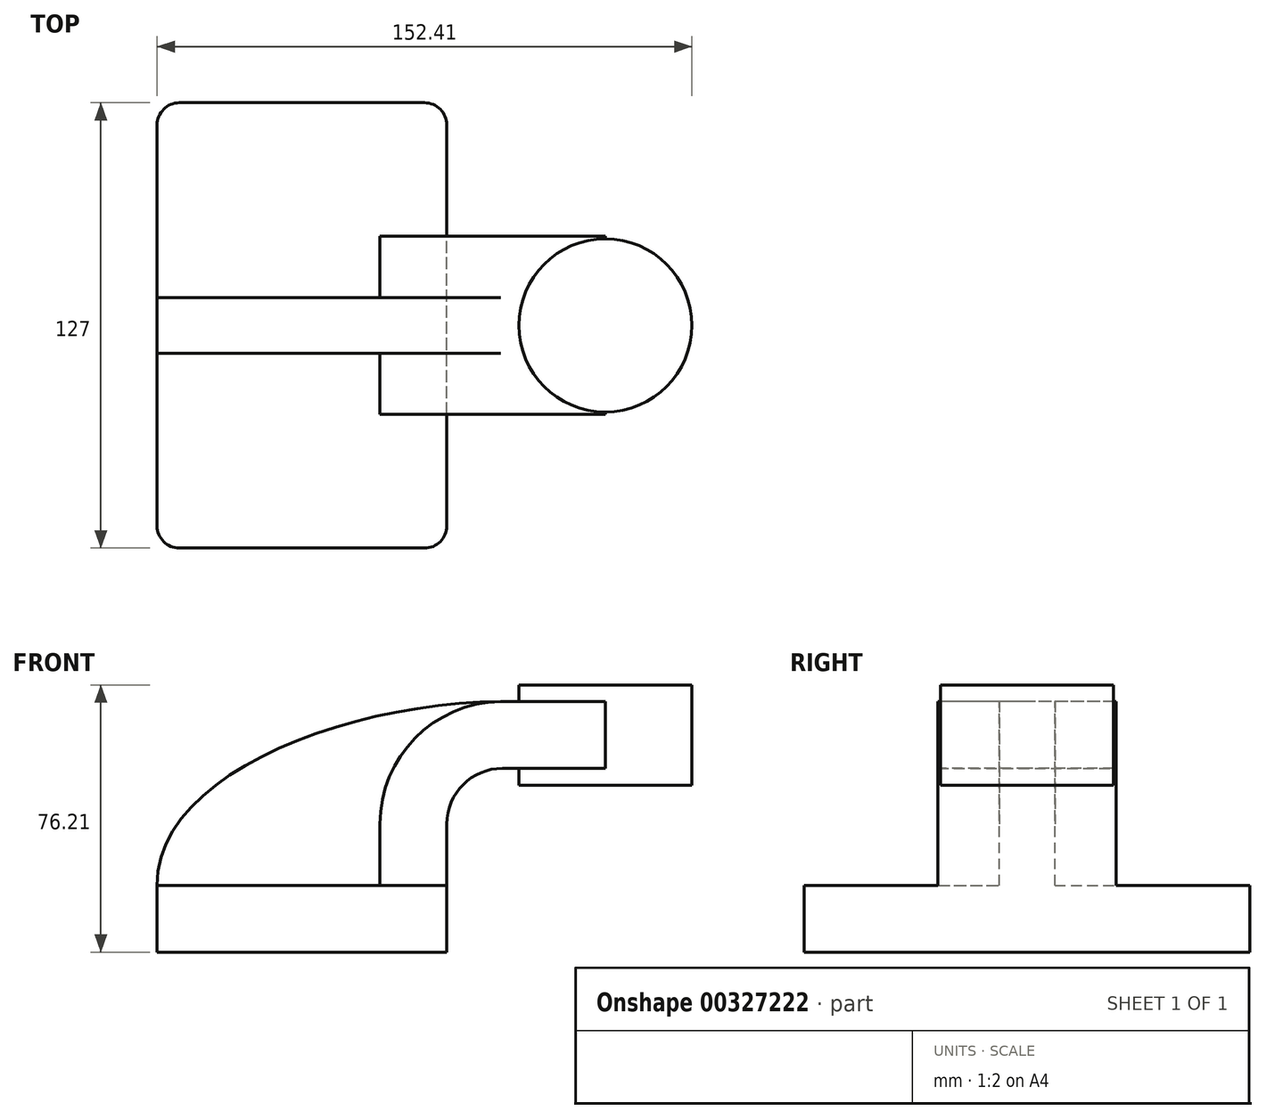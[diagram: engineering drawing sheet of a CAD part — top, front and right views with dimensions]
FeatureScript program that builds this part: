
annotation { "Feature Type Name" : "Feature", "Feature Type Description" : "" }
export const myFeature = defineFeature(function(context is Context, id is Id, definition is map)
    precondition{}
    {
        {
            var Q0;
            Q0=qCreatedBy(makeId("Front.planeOp"),FACE);
            var sketch = newSketch(context, id + "F0", { "sketchPlane" : qUnion([Q0])});
            skLineSegment(sketch, "E0.bottom", {"start": v(-41.28, 9.52) * mm, "end": v(41.27, 9.53) * mm});
            skLineSegment(sketch, "E0.top", {"start": v(-41.28, -9.53) * mm, "end": v(41.28, -9.53) * mm});
            skLineSegment(sketch, "E0.left", {"start": v(-41.28, 9.52) * mm, "end": v(-41.27, -9.53) * mm});
            skLineSegment(sketch, "E0.right", {"start": v(41.28, 9.53) * mm, "end": v(41.28, -9.52) * mm});
            skPoint(sketch, "E0.middle", {"position": v(0, 0) * mm});
            skLineSegment(sketch, "E1.bottom", {"start": v(60.33, 38.1) * mm, "end": v(111.12, 38.1) * mm});
            skLineSegment(sketch, "E1.top", {"start": v(60.32, 66.67) * mm, "end": v(111.12, 66.67) * mm});
            skLineSegment(sketch, "E1.left", {"start": v(60.33, 38.1) * mm, "end": v(60.32, 66.67) * mm});
            skLineSegment(sketch, "E1.right", {"start": v(111.13, 38.1) * mm, "end": v(111.12, 66.67) * mm});
            skPoint(sketch, "E1.middle", {"position": v(85.72, 52.39) * mm});
            skLineSegment(sketch, "E2", {"start": v(41.27, 9.53) * mm, "end": v(41.27, 27) * mm});
            skArc(sketch, "E3", {"start": v(41.27, 27) * mm, "mid": v(45.92, 38.23) * mm, "end": v(57.15, 42.88) * mm});
            skLineSegment(sketch, "E4", {"start": v(57.15, 42.88) * mm, "end": v(86.46, 42.88) * mm});
            skLineSegment(sketch, "E5.0", {"start": v(57.15, 61.93) * mm, "end": v(86.46, 61.93) * mm});
            skArc(sketch, "E5.1", {"start": v(22.23, 27) * mm, "mid": v(32.45, 51.7) * mm, "end": v(57.15, 61.93) * mm});
            skLineSegment(sketch, "E5.2", {"start": v(22.22, 9.53) * mm, "end": v(22.22, 27) * mm});
            skLineSegment(sketch, "E6", {"start": v(86.46, 38.1) * mm, "end": v(86.46, 66.67) * mm});
            skFitSpline(sketch, "E7", {"points": [v(-41.28, 9.53) * mm, v(57.15, 61.93) * mm], "startDerivative": vector(-0.4, 95.36) * mm, "endDerivative": vector(133.86, 0.83) * mm});
            skSolve(sketch);
        }
        {
            var Q0;
            Q0=makeQuery(id+"F0.imprint","IMPRINT",FACE,{"disambiguationData":[TD([[makeQuery(id+"F0.imprint","IMPRINT",EDGE,{"derivedFrom":sQuery(id+"F0.wireOp",EDGE,"E0.top")}),1.0]])]});
            extrude(context, id + "F1", {"entities" : qUnion([Q0]), "endBound" : BoundingType.SYMMETRIC, "depth" : 127 * mm});
        }
        {
            var Q0;
            {var subQ1=sQuery(id+"F0.wireOp",EDGE,"E2");Q0=makeQuery(id+"F0.imprint","IMPRINT",FACE,{"disambiguationData":[TD([[makeQuery(id+"F0.imprint","IMPRINT",EDGE,{"derivedFrom":subQ1}),1.0]])]});}
            var Q1;
            {var subQ0=sQuery(id+"F0.wireOp",EDGE,"E4");var subQ1=sQuery(id+"F0.wireOp",EDGE,"E1.left");var subQ2=makeQuery(id+"F0.imprint","INTERSECT",VERTEX,{"derivedFrom":[subQ1,subQ0]});Q1=makeQuery(id+"F0.imprint","IMPRINT",FACE,{"disambiguationData":[TD([[makeQuery(id+"F0.imprint","IMPRINT",EDGE,{"disambiguationData":[TD([[subQ2,-1.0]])],"derivedFrom":subQ1}),-1.0]])]});}
            extrude(context, id + "F2", {"entities" : qUnion([Q0, Q1]), "operationType" : NewBodyOperationType.ADD, "endBound" : BoundingType.SYMMETRIC, "depth" : 50.8 * mm});
        }
        {
            var Q0;
            {var subQ3=sQuery(id+"F0.wireOp",EDGE,"E5.2");Q0=makeQuery(id+"F0.imprint","IMPRINT",FACE,{"disambiguationData":[TD([[makeQuery(id+"F0.imprint","IMPRINT",EDGE,{"derivedFrom":subQ3}),1.0]])]});}
            extrude(context, id + "F3", {"entities" : qUnion([Q0]), "operationType" : NewBodyOperationType.ADD, "endBound" : BoundingType.SYMMETRIC, "depth" : 15.88 * mm});
        }
        {
            var Q0;
            {var subQ4=sQuery(id+"F0.wireOp",EDGE,"E1.right");Q0=makeQuery(id+"F0.imprint","IMPRINT",FACE,{"disambiguationData":[TD([[makeQuery(id+"F0.imprint","IMPRINT",EDGE,{"derivedFrom":subQ4}),1.0]])]});}
            var Q1;
            Q1=sQuery(id+"F0.wireOp",EDGE,"E6");
            revolve(context, id + "F4", {"operationType" : NewBodyOperationType.ADD, "entities" : qUnion([Q0]), "axis" : qUnion([Q1]), "revolveType" : RevolveType.FULL});
        }
        {
            var Q0;
            Q0=makeQuery(id+"F1.opExtrude","CAP_EDGE",EDGE,{"disambiguationData":[OSD([sQuery(id+"F0.wireOp",EDGE,"E0.left")])],"isStart":true});
            var Q1;
            Q1=makeQuery(id+"F1.opExtrude","CAP_EDGE",EDGE,{"disambiguationData":[OSD([sQuery(id+"F0.wireOp",EDGE,"E0.right")])],"isStart":true});
            var Q2;
            Q2=makeQuery(id+"F1.opExtrude","CAP_EDGE",EDGE,{"disambiguationData":[OSD([sQuery(id+"F0.wireOp",EDGE,"E0.right")])],"isStart":false});
            var Q3;
            Q3=makeQuery(id+"F1.opExtrude","CAP_EDGE",EDGE,{"disambiguationData":[OSD([sQuery(id+"F0.wireOp",EDGE,"E0.left")])],"isStart":false});
            fillet(context, id + "F5", {"entities" : qUnion([Q0, Q1, Q2, Q3]), "radius" : 6.35 * mm, "tangentPropagation" : true, "allowEdgeOverflow" : false});
        }
    });
